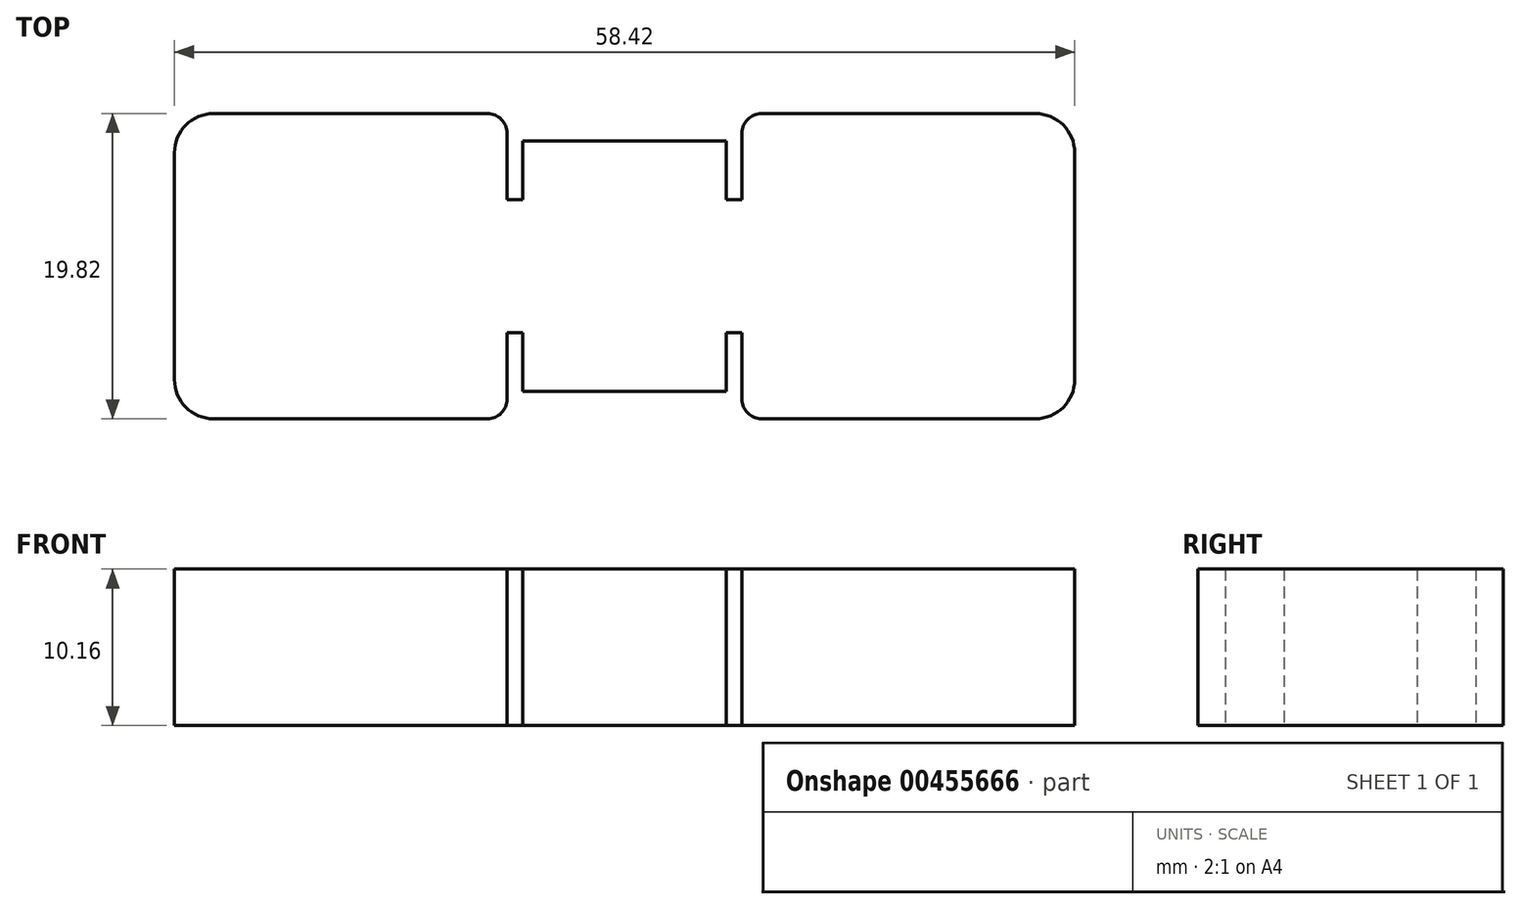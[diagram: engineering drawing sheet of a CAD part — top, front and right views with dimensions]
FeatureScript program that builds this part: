
annotation { "Feature Type Name" : "Feature", "Feature Type Description" : "" }
export const myFeature = defineFeature(function(context is Context, id is Id, definition is map)
    precondition{}
    {
        {
            var Q0;
            Q0=qCreatedBy(makeId("Top.planeOp"),FACE);
            var sketch = newSketch(context, id + "F0", { "sketchPlane" : qUnion([Q0])});
            skLineSegment(sketch, "E0", {"start": v(0, 0) * mm, "end": v(0, 8.13) * mm});
            skLineSegment(sketch, "E1", {"start": v(0, 0) * mm, "end": v(-29.21, 0) * mm});
            skLineSegment(sketch, "E2", {"start": v(-29.21, 0) * mm, "end": v(-29.21, 7.37) * mm});
            skLineSegment(sketch, "E3", {"start": v(-26.67, 9.9) * mm, "end": v(-8.89, 9.9) * mm});
            skLineSegment(sketch, "E4", {"start": v(-7.62, 8.64) * mm, "end": v(-7.62, 4.32) * mm});
            skLineSegment(sketch, "E5", {"start": v(-7.62, 4.32) * mm, "end": v(-6.6, 4.32) * mm});
            skLineSegment(sketch, "E6", {"start": v(-6.6, 4.32) * mm, "end": v(-6.6, 8.13) * mm});
            skLineSegment(sketch, "E7", {"start": v(-6.6, 8.13) * mm, "end": v(0, 8.13) * mm});
            skPoint(sketch, "E8.visualSharp", {"position": v(-29.21, 9.9) * mm});
            skArc(sketch, "E8.filletArc", {"start": v(-26.67, 9.9) * mm, "mid": v(-28.47, 9.16) * mm, "end": v(-29.21, 7.37) * mm});
            skPoint(sketch, "E9.visualSharp", {"position": v(-7.62, 9.9) * mm});
            skArc(sketch, "E9.filletArc", {"start": v(-7.62, 8.64) * mm, "mid": v(-8, 9.53) * mm, "end": v(-8.89, 9.9) * mm});
            skArc(sketch, "E10", {"start": v(-7.62, 5.33) * mm, "mid": v(-7.32, 4.62) * mm, "end": v(-6.6, 4.32) * mm});
            skSolve(sketch);
        }
        {
            var Q0;
            Q0=makeQuery(id+"F0.imprint","IMPRINT",FACE,{"disambiguationData":[TD([[makeQuery(id+"F0.imprint","IMPRINT",EDGE,{"derivedFrom":sQuery(id+"F0.wireOp",EDGE,"E0")}),1.0]])]});
            extrude(context, id + "F1", {"entities" : qUnion([Q0]), "depth" : 10.16 * mm});
        }
        {
            var Q0;
            Q0=makeQuery(id+"F1.opExtrude","SWEPT_BODY",BODY,{"disambiguationData":[OSD([sQuery(id+"F0.wireOp",EDGE,"E0"),sQuery(id+"F0.wireOp",EDGE,"E1"),sQuery(id+"F0.wireOp",EDGE,"E2"),sQuery(id+"F0.wireOp",EDGE,"E3"),sQuery(id+"F0.wireOp",EDGE,"E4"),sQuery(id+"F0.wireOp",EDGE,"E5"),sQuery(id+"F0.wireOp",EDGE,"E6"),sQuery(id+"F0.wireOp",EDGE,"E7"),sQuery(id+"F0.wireOp",EDGE,"E8.filletArc"),sQuery(id+"F0.wireOp",EDGE,"E9.filletArc")])]});
            var Q1;
            Q1=makeQuery(id+"F1.opExtrude","SWEPT_FACE",FACE,{"disambiguationData":[OSD([sQuery(id+"F0.wireOp",EDGE,"E0")])]});
            mirror(context, id + "F2", {"operationType" : NewBodyOperationType.ADD, "entities" : qUnion([Q0]), "mirrorPlane" : qUnion([Q1])});
        }
        {
            var Q0;
            Q0=makeQuery(id+"F1.opExtrude","SWEPT_BODY",BODY,{"disambiguationData":[OSD([sQuery(id+"F0.wireOp",EDGE,"E0"),sQuery(id+"F0.wireOp",EDGE,"E1"),sQuery(id+"F0.wireOp",EDGE,"E2"),sQuery(id+"F0.wireOp",EDGE,"E3"),sQuery(id+"F0.wireOp",EDGE,"E4"),sQuery(id+"F0.wireOp",EDGE,"E5"),sQuery(id+"F0.wireOp",EDGE,"E6"),sQuery(id+"F0.wireOp",EDGE,"E7"),sQuery(id+"F0.wireOp",EDGE,"E8.filletArc"),sQuery(id+"F0.wireOp",EDGE,"E9.filletArc")])]});
            var Q1;
            {var subQ0=makeQuery(id+"F1.opExtrude","SWEPT_FACE",FACE,{"disambiguationData":[OSD([sQuery(id+"F0.wireOp",EDGE,"E1")])]});Q1=makeQuery(id+"F2.boolean.opBoolean","MERGE",FACE,{"derivedFrom":[subQ0,makeQuery(id+"F2.opPattern","COPY",FACE,{"derivedFrom":subQ0,"instanceName":"1"})]});}
            mirror(context, id + "F3", {"operationType" : NewBodyOperationType.ADD, "entities" : qUnion([Q0]), "mirrorPlane" : qUnion([Q1])});
        }
    });
